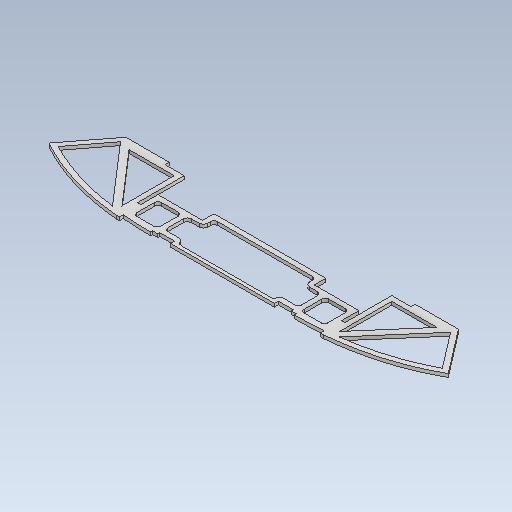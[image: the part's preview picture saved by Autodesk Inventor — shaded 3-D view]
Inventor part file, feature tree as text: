
AUTODESK INVENTOR PART (.ipt)
format: ipt  version: 2020.3 (Build 243373010, 373A)  size: 293,888 bytes
history: native  units: in
note: dims shown in document units (in); Inventor stores cm internally (conversion verified against a paired STEP export)
features: other x3, extrude x1, mirror x1, sketch x1
ambient origin geometry x8: Origin, YZ Plane, XZ Plane, XY Plane, X Axis, Y Axis, Z Axis, Center Point
bodies: Solid1 (feature_tree)
feature tree (6):
  other  "bulkhead_F1"
  other  "base_sketch.ipt"
  extrude  "Extrusion1"  Depth=0.0787in
  mirror  "Mirror1"
  other  "bulkhead_F1_plane"
  sketch  "Sketch2"  dims[d0=0.3937in d1=0.1181in d2=0.1181in d3=0.1181in d4=0.1575in d5=0.0787in d6=0.1181in d7=0.1181in d8=0.1181in d11=0.1181in d12=0.1181in d15=0.1181in d16=0.0787in d17=0.0787in d18=0.0in d19=0.1181in d21=0.0787in d23=0.2362in d24=0.2362in d25=0.0472in d26=0.0472in d27=0.7902in d28=0.1181in d29=0.0079in d30=0.1969in]
